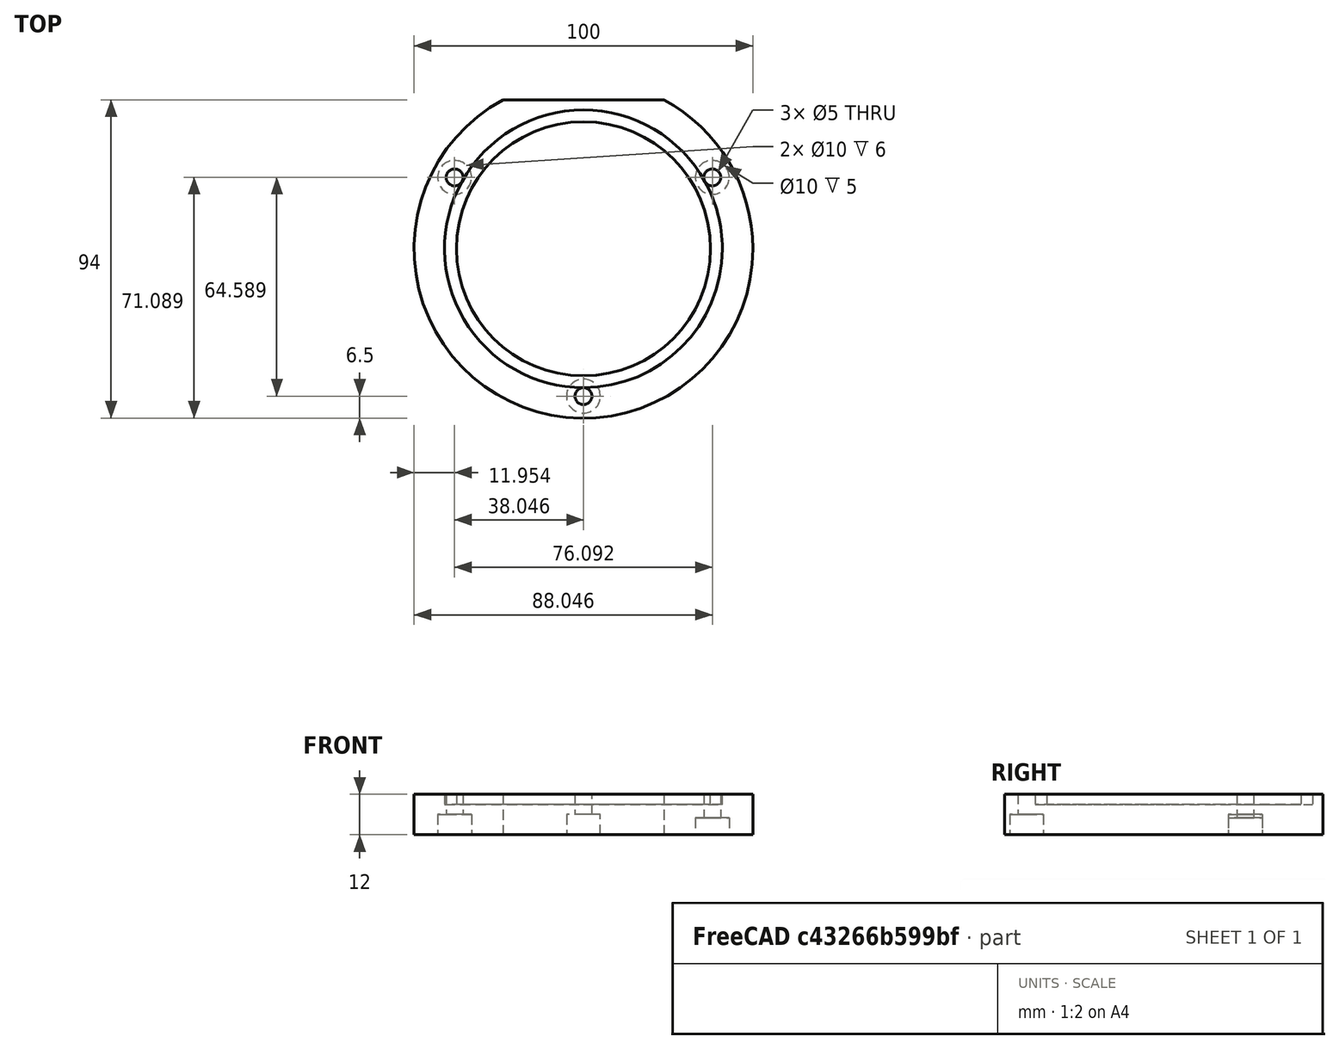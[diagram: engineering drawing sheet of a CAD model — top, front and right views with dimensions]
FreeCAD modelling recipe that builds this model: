
FCSTD DOCUMENT  (FreeCAD 0.20R)
Label: PhilipsXL30_Blindflange_100_TopBack
License: All rights reserved
LicenseURL: http://en.wikipedia.org/wiki/All_rights_reserved
objects: TechDraw::DrawViewDimension×18, Part::Cylinder×9, Part::Compound×6, Part::Cut×5, TechDraw::DrawProjGroupItem×3, Part::Box×1, TechDraw::DrawSVGTemplate×1, TechDraw::DrawProjGroup×1, TechDraw::DrawViewSection×1, TechDraw::DrawPage×1
note: 21 computed .brp shape members not serialized (recipe doc carries the construction recipe); baked Part::Feature solids carry a one-line shape summary decoded from their .brp

FEATURE [Part::Cylinder] Cylinder
  Angle = 360
  AttacherType = Attacher::AttachEngine3D
  FirstAngle = 0
  Height = 12
  Radius = 50
  SecondAngle = 0
FEATURE [Part::Cylinder] Cylinder001
  Angle = 360
  AttacherType = Attacher::AttachEngine3D
  FirstAngle = 0
  Height = 3
  Radius = 37.5
  SecondAngle = 0
FEATURE [Part::Cylinder] Cylinder002
  Angle = 360
  AttacherType = Attacher::AttachEngine3D
  FirstAngle = 0
  Height = 3
  Radius = 41
  SecondAngle = 0
FEATURE [Part::Cut] Cut
  Base = -> Cylinder002
  Placement = pos=(0,0,9) rot=(0,0,1;0rad)
  Tool = -> Cylinder001
FEATURE [Part::Cut] Cut001
  Base = -> Cylinder
  Tool = -> Cut
FEATURE [Part::Box] Box  label="Cube"
  AttacherType = Attacher::AttachEngine3D
  Height = 12
  Length = 200
  Placement = pos=(-100,44,0) rot=(0,0,1;0rad)
  Width = 100
FEATURE [Part::Cut] Cut002
  Base = -> Cut001
  Tool = -> Box
FEATURE [Part::Cylinder] Cylinder003
  Angle = 360
  AttacherType = Attacher::AttachEngine3D
  FirstAngle = 0
  Height = 12
  Placement = pos=(0,-43.5,0) rot=(0,0,1;0rad)
  Radius = 2.5
  SecondAngle = 0
FEATURE [Part::Cylinder] Cylinder004
  Angle = 360
  AttacherType = Attacher::AttachEngine3D
  FirstAngle = 0
  Height = 12
  Placement = pos=(0,-43.5,0) rot=(0,0,1;0rad)
  Radius = 2.5
  SecondAngle = 0
FEATURE [Part::Cylinder] Cylinder005
  Angle = 360
  AttacherType = Attacher::AttachEngine3D
  FirstAngle = 0
  Height = 12
  Placement = pos=(0,-43.5,0) rot=(0,0,1;0rad)
  Radius = 2.5
  SecondAngle = 0
FEATURE [Part::Compound] Compound
  Links = -> [Cylinder004]
  Placement = pos=(0,0,0) rot=(0,0,1;2.07694rad)
FEATURE [Part::Compound] Compound001
  Links = -> [Cylinder005]
  Placement = pos=(0,0,0) rot=(0,0,1;-2.07694rad)
FEATURE [Part::Compound] Compound002
  Links = -> [Cylinder003,Compound,Compound001]
FEATURE [Part::Cut] Cut003
  Base = -> Cut002
  Tool = -> Compound002
FEATURE [Part::Cylinder] Cylinder006
  Angle = 360
  AttacherType = Attacher::AttachEngine3D
  FirstAngle = 0
  Height = 6
  Placement = pos=(0,-43.5,0) rot=(0,0,1;0rad)
  Radius = 5
  SecondAngle = 0
FEATURE [Part::Cylinder] Cylinder007
  Angle = 360
  AttacherType = Attacher::AttachEngine3D
  FirstAngle = 0
  Height = 5
  Placement = pos=(0,-43.5,0) rot=(0,0,1;0rad)
  Radius = 5
  SecondAngle = 0
FEATURE [Part::Compound] Compound003
  Links = -> [Cylinder007]
  Placement = pos=(0,0,0) rot=(0,0,1;2.07694rad)
FEATURE [Part::Cylinder] Cylinder008
  Angle = 360
  AttacherType = Attacher::AttachEngine3D
  FirstAngle = 0
  Height = 6
  Placement = pos=(0,-43.5,0) rot=(0,0,1;0rad)
  Radius = 5
  SecondAngle = 0
FEATURE [Part::Compound] Compound004
  Links = -> [Cylinder008]
  Placement = pos=(0,0,0) rot=(0,0,-1;2.07694rad)
FEATURE [Part::Compound] Compound005
  Links = -> [Cylinder006,Compound003,Compound004]
FEATURE [Part::Cut] Cut004  label="XL30TopBackFlange100"
  Base = -> Cut003
  Tool = -> Compound005
FEATURE [TechDraw::DrawSVGTemplate] Template
  EditableTexts = Designed_by_Name=Thomas Spielauer; Drawing_number=1; FC-Date=2023-12-18; FC-SC=mm; FC-Title=XL30 compatible 100m flange; Subtitle=Back side top left
  Height = 210
  Orientation = 1
  Width = 297
FEATURE [TechDraw::DrawProjGroupItem] ProjItem  label="Front"
  CoarseView = false
  Direction = (0,0,1)
  Focus = 100
  HardHidden = false
  IsoCount = 0
  IsoHidden = false
  IsoVisible = false
  LockPosition = true
  Perspective = false
  Rotation = 0
  RotationVector = (-1,0,0)
  ScaleType = 2
  SeamHidden = false
  SeamVisible = true
  SmoothHidden = false
  SmoothVisible = true
  Source = -> [Cut004]
  Type = 0
  X = 0
  XDirection = (-1,0,0)
  Y = 0
FEATURE [TechDraw::DrawProjGroupItem] ProjItem002  label="Rear"
  CoarseView = false
  Direction = (0,0,-1)
  Focus = 100
  HardHidden = false
  IsoCount = 0
  IsoHidden = false
  IsoVisible = false
  LockPosition = false
  Perspective = false
  Rotation = 0
  RotationVector = (1,0,0)
  ScaleType = 2
  SeamHidden = false
  SeamVisible = true
  SmoothHidden = false
  SmoothVisible = true
  Source = -> [Cut004]
  Type = 3
  X = 112.613
  XDirection = (1,0,0)
  Y = 0
FEATURE [TechDraw::DrawProjGroupItem] ProjItem003  label="Top"
  CoarseView = false
  Direction = (0,-1,0)
  Focus = 100
  HardHidden = false
  IsoCount = 0
  IsoHidden = false
  IsoVisible = false
  LockPosition = false
  Perspective = false
  Rotation = 0
  RotationVector = (1,0,0)
  ScaleType = 2
  SeamHidden = false
  SeamVisible = true
  SmoothHidden = false
  SmoothVisible = true
  Source = -> [Cut004]
  Type = 4
  X = 0
  XDirection = (-1,0,0)
  Y = -112.049
FEATURE [TechDraw::DrawProjGroup] ProjGroup
  Anchor = -> ProjItem
  AutoDistribute = false
  LockPosition = false
  ProjectionType = 0
  Rotation = 0
  ScaleType = 0
  Source = -> [Cut004]
  Views = -> [ProjItem,ProjItem002,ProjItem003]
  X = 71.1104
  Y = 147.781
  spacingX = 15
  spacingY = 15
FEATURE [TechDraw::DrawViewDimension] Dimension
  AngleOverride = false
  Arbitrary = false
  ArbitraryTolerances = false
  EqualTolerance = true
  ExtensionAngle = 0
  FormatSpec = ⌀%.2w
  FormatSpecOverTolerance = %+.2w
  FormatSpecUnderTolerance = %+.2w
  Inverted = false
  LineAngle = 0
  LockPosition = false
  MeasureType = 1
  OverTolerance = 0
  References2D = -> [ProjItem]
  Rotation = 0
  ScaleType = 0
  TheoreticalExact = false
  Type = 5
  UnderTolerance = 0
  X = 32.6688
  Y = 47.2408
FEATURE [TechDraw::DrawViewDimension] Dimension001
  AngleOverride = false
  Arbitrary = false
  ArbitraryTolerances = false
  EqualTolerance = true
  ExtensionAngle = 0
  FormatSpec = ⌀%.2w
  FormatSpecOverTolerance = %+.2w
  FormatSpecUnderTolerance = %+.2w
  Inverted = false
  LineAngle = 0
  LockPosition = false
  MeasureType = 1
  OverTolerance = 0
  References2D = -> [ProjItem]
  Rotation = 0
  ScaleType = 0
  TheoreticalExact = false
  Type = 5
  UnderTolerance = 0
  X = 51.305
  Y = 16.9487
FEATURE [TechDraw::DrawViewDimension] Dimension002
  AngleOverride = false
  Arbitrary = false
  ArbitraryTolerances = false
  EqualTolerance = true
  ExtensionAngle = 0
  FormatSpec = ⌀%.2w
  FormatSpecOverTolerance = %+.2w
  FormatSpecUnderTolerance = %+.2w
  Inverted = false
  LineAngle = 0
  LockPosition = false
  MeasureType = 1
  OverTolerance = 0
  References2D = -> [ProjItem]
  Rotation = 0
  ScaleType = 0
  TheoreticalExact = false
  Type = 5
  UnderTolerance = 0
  X = 54.375
  Y = 11.2918
FEATURE [TechDraw::DrawViewDimension] Dimension003
  AngleOverride = false
  Arbitrary = false
  ArbitraryTolerances = false
  EqualTolerance = true
  ExtensionAngle = 0
  FormatSpec = ⌀%.2w
  FormatSpecOverTolerance = %+.2w
  FormatSpecUnderTolerance = %+.2w
  Inverted = false
  LineAngle = 0
  LockPosition = false
  MeasureType = 1
  OverTolerance = 0
  References2D = -> [ProjItem]
  Rotation = 0
  ScaleType = 0
  TheoreticalExact = false
  Type = 5
  UnderTolerance = 0
  X = 40.665
  Y = 45.6731
FEATURE [TechDraw::DrawViewDimension] Dimension004
  AngleOverride = false
  Arbitrary = false
  ArbitraryTolerances = false
  EqualTolerance = true
  ExtensionAngle = 0
  FormatSpec = ⌀%.2w (3x)
  FormatSpecOverTolerance = %+.2w
  FormatSpecUnderTolerance = %+.2w
  Inverted = false
  LineAngle = 0
  LockPosition = false
  MeasureType = 1
  OverTolerance = 0
  References2D = -> [ProjItem]
  Rotation = 0
  ScaleType = 0
  TheoreticalExact = false
  Type = 5
  UnderTolerance = 0
  X = -41.9055
  Y = 45.1875
FEATURE [TechDraw::DrawViewDimension] Dimension005
  AngleOverride = false
  Arbitrary = false
  ArbitraryTolerances = false
  EqualTolerance = true
  ExtensionAngle = 0
  FormatSpec = %.2w
  FormatSpecOverTolerance = %+.2w
  FormatSpecUnderTolerance = %+.2w
  Inverted = false
  LineAngle = 0
  LockPosition = false
  MeasureType = 1
  OverTolerance = 0
  References2D = -> [ProjItem]
  Rotation = 0
  ScaleType = 0
  TheoreticalExact = false
  Type = 6
  UnderTolerance = 0
  X = -13.992
  Y = -14.5232
FEATURE [TechDraw::DrawViewDimension] Dimension006
  AngleOverride = false
  Arbitrary = false
  ArbitraryTolerances = false
  EqualTolerance = true
  ExtensionAngle = 0
  FormatSpec = %.2w
  FormatSpecOverTolerance = %+.2w
  FormatSpecUnderTolerance = %+.2w
  Inverted = false
  LineAngle = 0
  LockPosition = false
  MeasureType = 1
  OverTolerance = 0
  References2D = -> [ProjItem]
  Rotation = 0
  ScaleType = 0
  TheoreticalExact = false
  Type = 6
  UnderTolerance = 0
  X = 15.1619
  Y = -18.6647
FEATURE [TechDraw::DrawViewDimension] Dimension007
  AngleOverride = false
  Arbitrary = false
  ArbitraryTolerances = false
  EqualTolerance = true
  ExtensionAngle = 0
  FormatSpec = ⌀%.2w
  FormatSpecOverTolerance = %+.2w
  FormatSpecUnderTolerance = %+.2w
  Inverted = false
  LineAngle = 0
  LockPosition = false
  MeasureType = 1
  OverTolerance = 0
  References2D = -> [ProjItem002]
  Rotation = 0
  ScaleType = 0
  TheoreticalExact = false
  Type = 5
  UnderTolerance = 0
  X = 30.2276
  Y = 46.2839
FEATURE [TechDraw::DrawViewDimension] Dimension008
  AngleOverride = false
  Arbitrary = false
  ArbitraryTolerances = false
  EqualTolerance = true
  ExtensionAngle = 0
  FormatSpec = %.2w
  FormatSpecOverTolerance = %+.2w
  FormatSpecUnderTolerance = %+.2w
  Inverted = false
  LineAngle = 0
  LockPosition = false
  MeasureType = 1
  OverTolerance = 0
  References2D = -> [ProjItem002]
  Rotation = 0
  ScaleType = 0
  TheoreticalExact = false
  Type = 1
  UnderTolerance = 0
  X = 1.73891
  Y = -33.3071
FEATURE [TechDraw::DrawViewDimension] Dimension009
  AngleOverride = false
  Arbitrary = false
  ArbitraryTolerances = false
  EqualTolerance = true
  ExtensionAngle = 0
  FormatSpec = %.2w
  FormatSpecOverTolerance = %+.2w
  FormatSpecUnderTolerance = %+.2w
  Inverted = false
  LineAngle = 0
  LockPosition = false
  MeasureType = 1
  OverTolerance = 0
  References2D = -> [ProjItem002]
  Rotation = 0
  ScaleType = 0
  TheoreticalExact = false
  Type = 2
  UnderTolerance = 0
  X = -7.34944
  Y = -21.677
FEATURE [TechDraw::DrawViewDimension] Dimension010
  AngleOverride = false
  Arbitrary = false
  ArbitraryTolerances = false
  EqualTolerance = true
  ExtensionAngle = 0
  FormatSpec = %.2w
  FormatSpecOverTolerance = %+.2w
  FormatSpecUnderTolerance = %+.2w
  Inverted = false
  LineAngle = 0
  LockPosition = false
  MeasureType = 1
  OverTolerance = 0
  References2D = -> [ProjItem003]
  Rotation = 0
  ScaleType = 0
  TheoreticalExact = false
  Type = 2
  UnderTolerance = 0
  X = 58.602
  Y = 14.0619
FEATURE [TechDraw::DrawViewSection] SectionView  label="Section  - "
  BaseView = -> ProjItem002
  CoarseView = false
  CutSurfaceDisplay = 2
  Direction = (-1,0,0)
  FileGeomPattern = <path>
  FileHatchPattern = <path>
  Focus = 100
  FuseBeforeCut = false
  HardHidden = false
  HatchScale = 1
  IsoCount = 0
  IsoHidden = false
  IsoVisible = false
  LockPosition = false
  NameGeomPattern = Diamond
  Perspective = false
  Rotation = 0
  ScaleType = 2
  SeamHidden = false
  SeamVisible = true
  SectionDirection = 0
  SectionNormal = (-1,0,0)
  SectionOrigin = (0.044,-2.97,6)
  SmoothHidden = false
  SmoothVisible = true
  Source = -> [Cut004]
  X = 264.208
  XDirection = (0,0,-1)
  Y = 135.168
FEATURE [TechDraw::DrawViewDimension] Dimension011
  AngleOverride = false
  Arbitrary = false
  ArbitraryTolerances = false
  EqualTolerance = true
  ExtensionAngle = 0
  FormatSpec = %.2w
  FormatSpecOverTolerance = %+.2w
  FormatSpecUnderTolerance = %+.2w
  Inverted = false
  LineAngle = 0
  LockPosition = false
  MeasureType = 1
  OverTolerance = 0
  References2D = -> [SectionView]
  Rotation = 0
  ScaleType = 0
  TheoreticalExact = false
  Type = 2
  UnderTolerance = 0
  X = 15.2511
  Y = 31.7095
FEATURE [TechDraw::DrawViewDimension] Dimension012
  AngleOverride = false
  Arbitrary = false
  ArbitraryTolerances = false
  EqualTolerance = true
  ExtensionAngle = 0
  FormatSpec = %.2w
  FormatSpecOverTolerance = %+.2w
  FormatSpecUnderTolerance = %+.2w
  Inverted = false
  LineAngle = 0
  LockPosition = false
  MeasureType = 1
  OverTolerance = 0
  References2D = -> [SectionView]
  Rotation = 0
  ScaleType = 0
  TheoreticalExact = false
  Type = 0
  UnderTolerance = 0
  X = -15.1499
  Y = 49.9924
FEATURE [TechDraw::DrawViewDimension] Dimension013
  AngleOverride = false
  Arbitrary = false
  ArbitraryTolerances = false
  EqualTolerance = true
  ExtensionAngle = 0
  FormatSpec = %.2w
  FormatSpecOverTolerance = %+.2w
  FormatSpecUnderTolerance = %+.2w
  Inverted = false
  LineAngle = 0
  LockPosition = false
  MeasureType = 1
  OverTolerance = 0
  References2D = -> [SectionView]
  Rotation = 0
  ScaleType = 0
  TheoreticalExact = false
  Type = 0
  UnderTolerance = 0
  X = -15.7993
  Y = -26.0238
FEATURE [TechDraw::DrawViewDimension] Dimension014
  AngleOverride = false
  Arbitrary = false
  ArbitraryTolerances = false
  EqualTolerance = true
  ExtensionAngle = 0
  FormatSpec = %.2w
  FormatSpecOverTolerance = %+.2w
  FormatSpecUnderTolerance = %+.2w
  Inverted = false
  LineAngle = 0
  LockPosition = false
  MeasureType = 1
  OverTolerance = 0
  References2D = -> [SectionView]
  Rotation = 0
  ScaleType = 0
  TheoreticalExact = false
  Type = 0
  UnderTolerance = 0
  X = 7.4555
  Y = -57.2723
FEATURE [TechDraw::DrawViewDimension] Dimension015
  AngleOverride = false
  Arbitrary = false
  ArbitraryTolerances = false
  EqualTolerance = true
  ExtensionAngle = 0
  FormatSpec = %.2w
  FormatSpecOverTolerance = %+.2w
  FormatSpecUnderTolerance = %+.2w
  Inverted = false
  LineAngle = 0
  LockPosition = false
  MeasureType = 1
  OverTolerance = 0
  References2D = -> [SectionView]
  Rotation = 0
  ScaleType = 0
  TheoreticalExact = false
  Type = 0
  UnderTolerance = 0
  X = 12.3852
  Y = 64.439
FEATURE [TechDraw::DrawViewDimension] Dimension016
  AngleOverride = false
  Arbitrary = false
  ArbitraryTolerances = false
  EqualTolerance = true
  ExtensionAngle = 0
  FormatSpec = %.2w
  FormatSpecOverTolerance = %+.2w
  FormatSpecUnderTolerance = %+.2w
  Inverted = false
  LineAngle = 0
  LockPosition = false
  MeasureType = 1
  OverTolerance = 0
  References2D = -> [SectionView]
  Rotation = 0
  ScaleType = 0
  TheoreticalExact = false
  Type = 0
  UnderTolerance = 0
  X = -7.31285
  Y = 57.1646
FEATURE [TechDraw::DrawViewDimension] Dimension017
  AngleOverride = false
  Arbitrary = false
  ArbitraryTolerances = false
  EqualTolerance = true
  ExtensionAngle = 0
  FormatSpec = %.2w
  FormatSpecOverTolerance = %+.2w
  FormatSpecUnderTolerance = %+.2w
  Inverted = false
  LineAngle = 0
  LockPosition = false
  MeasureType = 1
  OverTolerance = 0
  References2D = -> [ProjItem003]
  Rotation = 0
  ScaleType = 0
  TheoreticalExact = false
  Type = 0
  UnderTolerance = 0
  X = -4.76361
  Y = 18.035
FEATURE [TechDraw::DrawPage] Page
  KeepUpdated = true
  NextBalloonIndex = 1
  ProjectionType = 0
  Template = -> Template
  Views = -> [ProjGroup,Dimension,Dimension001,Dimension002,Dimension003,Dimension004,Dimension005,Dimension006,Dimension007,Dimension008,Dimension009,Dimension010,SectionView,Dimension011,Dimension012,Dimension013,Dimension014,Dimension015,Dimension016,Dimension017]
note: 2 file-system paths scrubbed to <path> (originals preserved in the JSON sidecar)
